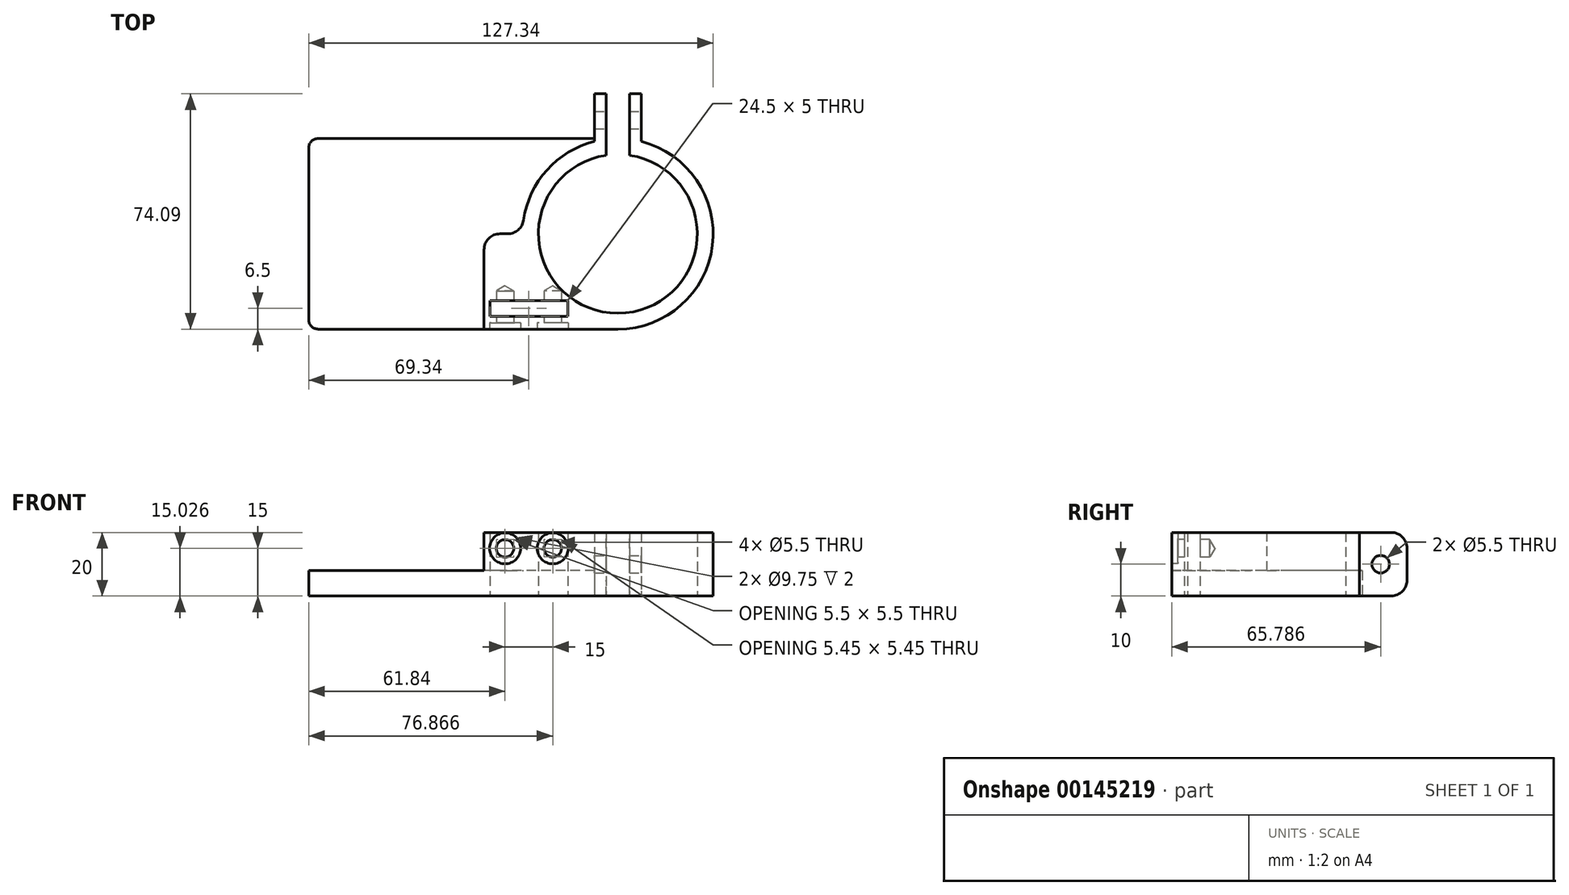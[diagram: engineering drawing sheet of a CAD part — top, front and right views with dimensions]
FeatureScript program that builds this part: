
annotation { "Feature Type Name" : "Feature", "Feature Type Description" : "" }
export const myFeature = defineFeature(function(context is Context, id is Id, definition is map)
    precondition{}
    {
        {
            var Q0;
            Q0=qCreatedBy(makeId("Top.planeOp"),FACE);
            var sketch = newSketch(context, id + "F0", { "sketchPlane" : qUnion([Q0])});
            skArc(sketch, "E0", {"start": v(-7.34, 29.09) * mm, "mid": v(0, -30) * mm, "end": v(7.34, 29.09) * mm});
            skArc(sketch, "E1.0", {"start": v(-3.67, 24.73) * mm, "mid": v(0, -25) * mm, "end": v(3.67, 24.73) * mm});
            skLineSegment(sketch, "E2", {"start": v(-7.34, 30) * mm, "end": v(-94.34, 30) * mm});
            skLineSegment(sketch, "E3", {"start": v(-97.34, 27) * mm, "end": v(-97.34, -27) * mm});
            skLineSegment(sketch, "E4", {"start": v(-94.34, -30) * mm, "end": v(0, -30) * mm});
            skLineSegment(sketch, "E5", {"start": v(-7.34, 29.09) * mm, "end": v(-7.34, 44.09) * mm});
            skLineSegment(sketch, "E6", {"start": v(-7.34, 44.09) * mm, "end": v(-3.67, 44.09) * mm});
            skLineSegment(sketch, "E7.MirrorCS", {"start": v(7.34, 29.09) * mm, "end": v(7.34, 44.09) * mm});
            skLineSegment(sketch, "E8.MirrorCS", {"start": v(7.34, 44.09) * mm, "end": v(3.67, 44.09) * mm});
            skPoint(sketch, "E9.orphan", {"position": v(0, 30) * mm});
            skPoint(sketch, "E10.orphan", {"position": v(-7.34, 23.9) * mm});
            skPoint(sketch, "E11.orphan", {"position": v(7.34, 23.9) * mm});
            skLineSegment(sketch, "E12", {"start": v(-3.67, 44.09) * mm, "end": v(-3.67, 24.73) * mm});
            skLineSegment(sketch, "E13.MirrorCS", {"start": v(3.67, 44.09) * mm, "end": v(3.67, 24.73) * mm});
            skPoint(sketch, "E14.orphan", {"position": v(0, 44.09) * mm});
            skPoint(sketch, "E15.visualSharp", {"position": v(-97.34, 30) * mm});
            skArc(sketch, "E15.filletArc", {"start": v(-94.34, 30) * mm, "mid": v(-96.46, 29.12) * mm, "end": v(-97.34, 27) * mm});
            skPoint(sketch, "E16.visualSharp", {"position": v(-97.34, -30) * mm});
            skArc(sketch, "E16.filletArc", {"start": v(-97.34, -27) * mm, "mid": v(-96.46, -29.12) * mm, "end": v(-94.34, -30) * mm});
            skPoint(sketch, "E17.start.orphan", {"position": v(-30, 0) * mm});
            skLineSegment(sketch, "E18", {"start": v(-30, 0) * mm, "end": v(-42.11, 0) * mm});
            skLineSegment(sketch, "E19", {"start": v(-42.11, 0) * mm, "end": v(-42.11, -30) * mm});
            skSolve(sketch);
        }
        {
            var Q0;
            Q0=makeQuery(id+"F0.imprint","IMPRINT",FACE,{"disambiguationData":[TD([[makeQuery(id+"F0.imprint","IMPRINT",EDGE,{"derivedFrom":sQuery(id+"F0.wireOp",EDGE,"E1.0")}),-1.0]])]});
            extrude(context, id + "F1", {"entities" : qUnion([Q0]), "depth" : 20 * mm});
        }
        {
            var Q0;
            Q0 = qSketchRegion(id + "F0", true);
            extrude(context, id + "F2", {"entities" : qUnion([Q0]), "operationType" : NewBodyOperationType.ADD, "depth" : 8 * mm});
        }
        {
            var Q0;
            {var subQ3=sQuery(id+"F0.wireOp",EDGE,"E18");Q0=makeQuery(id+"F0.imprint","IMPRINT",FACE,{"disambiguationData":[TD([[makeQuery(id+"F0.imprint","IMPRINT",EDGE,{"derivedFrom":subQ3}),1.0]])]});}
            extrude(context, id + "F3", {"entities" : qUnion([Q0]), "operationType" : NewBodyOperationType.ADD, "depth" : 20 * mm});
        }
        {
            var Q0;
            Q0=makeQuery(id+"F1.opExtrude","CAP_EDGE",EDGE,{"disambiguationData":[OSD([sQuery(id+"F0.wireOp",EDGE,"E8.MirrorCS")])],"isStart":true});
            var Q1;
            Q1=makeQuery(id+"F1.opExtrude","CAP_EDGE",EDGE,{"disambiguationData":[OSD([sQuery(id+"F0.wireOp",EDGE,"E6")])],"isStart":true});
            var Q2;
            Q2=makeQuery(id+"F1.opExtrude","CAP_EDGE",EDGE,{"disambiguationData":[OSD([sQuery(id+"F0.wireOp",EDGE,"E6")])],"isStart":false});
            var Q3;
            Q3=makeQuery(id+"F1.opExtrude","CAP_EDGE",EDGE,{"disambiguationData":[OSD([sQuery(id+"F0.wireOp",EDGE,"E8.MirrorCS")])],"isStart":false});
            fillet(context, id + "F4", {"entities" : qUnion([Q0, Q1, Q2, Q3]), "radius" : 5 * mm, "tangentPropagation" : true, "allowEdgeOverflow" : false});
        }
        {
            var Q0;
            Q0=makeQuery(id+"F1.opExtrude","SWEPT_FACE",FACE,{"disambiguationData":[OSD([sQuery(id+"F0.wireOp",EDGE,"E7.MirrorCS")])]});
            var sketch = newSketch(context, id + "F5", { "sketchPlane" : qUnion([Q0])});
            skPoint(sketch, "E20", {"position": v(35.79, 10) * mm});
            skPoint(sketch, "E20.positionSnap0", {"position": v(29.09, 10) * mm});
            skSolve(sketch);
        }
        {
            var Q0;
            Q0=sQuery(id+"F5.wireOp",VERTEX,"E20");
            var Q1;
            Q1=makeQuery(id+"F1.opExtrude","SWEPT_BODY",BODY,{"disambiguationData":[OSD([sQuery(id+"F0.wireOp",EDGE,"E0"),sQuery(id+"F0.wireOp",EDGE,"E1.0"),sQuery(id+"F0.wireOp",EDGE,"E5"),sQuery(id+"F0.wireOp",EDGE,"E6"),sQuery(id+"F0.wireOp",EDGE,"E7.MirrorCS"),sQuery(id+"F0.wireOp",EDGE,"E8.MirrorCS"),sQuery(id+"F0.wireOp",EDGE,"E12"),sQuery(id+"F0.wireOp",EDGE,"E13.MirrorCS")])]});
            hole(context, id + "F6", {"style" : HoleStyle.SIMPLE, "endStyle" : HoleEndStyle.THROUGH, "holeDiameter" : 5.5 * mm, "locations" : qUnion([Q0]), "scope" : qUnion([Q1]), "isTappedThrough" : true});
        }
        {
            var Q0;
            Q0=makeQuery(id+"F3.opExtrude","SWEPT_EDGE",EDGE,{"disambiguationData":[OSD([sQuery(id+"F0.wireOp",EDGE,"E18"),sQuery(id+"F0.wireOp",EDGE,"E19")])]});
            var Q1;
            Q1=makeQuery(id+"F3.opExtrude","SWEPT_EDGE",EDGE,{"disambiguationData":[OSD([sQuery(id+"F0.wireOp",EDGE,"E0"),sQuery(id+"F0.wireOp",EDGE,"E18")])]});
            fillet(context, id + "F7", {"entities" : qUnion([Q0, Q1]), "radius" : 5 * mm, "tangentPropagation" : true, "allowEdgeOverflow" : false});
        }
        {
            var Q0;
            {var subQ0=sQuery(id+"F0.wireOp",EDGE,"E13.MirrorCS");var subQ1=sQuery(id+"F0.wireOp",EDGE,"E12");var subQ2=sQuery(id+"F0.wireOp",EDGE,"E8.MirrorCS");var subQ3=sQuery(id+"F0.wireOp",EDGE,"E7.MirrorCS");var subQ4=sQuery(id+"F0.wireOp",EDGE,"E6");var subQ5=sQuery(id+"F0.wireOp",EDGE,"E5");var subQ6=sQuery(id+"F0.wireOp",EDGE,"E1.0");var subQ7=sQuery(id+"F0.wireOp",EDGE,"E0");Q0=makeQuery(id+"F2.boolean.opBoolean","MERGE",FACE,{"derivedFrom":[makeQuery(id+"F1.opExtrude","CAP_FACE",FACE,{"disambiguationData":[OSD([subQ7,subQ6,subQ5,subQ4,subQ3,subQ2,subQ1,subQ0])],"isStart":true}),makeQuery(id+"F2.opExtrude","CAP_FACE",FACE,{"disambiguationData":[OSD([subQ7,subQ6,sQuery(id+"F0.wireOp",EDGE,"E2"),sQuery(id+"F0.wireOp",EDGE,"E3"),sQuery(id+"F0.wireOp",EDGE,"E4"),subQ5,subQ4,subQ3,subQ2,subQ1,subQ0,sQuery(id+"F0.wireOp",EDGE,"E15.filletArc"),sQuery(id+"F0.wireOp",EDGE,"E16.filletArc")])],"isStart":true})]});}
            var sketch = newSketch(context, id + "F8", { "sketchPlane" : qUnion([Q0])});
            skLineSegment(sketch, "E21.bottom", {"start": v(-40.25, 26) * mm, "end": v(-15.75, 26) * mm});
            skLineSegment(sketch, "E21.top", {"start": v(-40.25, 21) * mm, "end": v(-15.75, 21) * mm});
            skLineSegment(sketch, "E21.left", {"start": v(-40.25, 26) * mm, "end": v(-40.25, 21) * mm});
            skLineSegment(sketch, "E21.right", {"start": v(-15.75, 26) * mm, "end": v(-15.75, 21) * mm});
            skLineSegment(sketch, "E22", {"start": v(-28, 43.68) * mm, "end": v(-28, 10.05) * mm, "construction": true});
            skPoint(sketch, "E22.startSnap0", {"position": v(-28, 26) * mm});
            skSolve(sketch);
        }
        {
            var Q0;
            Q0=makeQuery(id+"F8.imprint","IMPRINT",FACE,{"disambiguationData":[TD([[makeQuery(id+"F8.imprint","IMPRINT",EDGE,{"derivedFrom":sQuery(id+"F8.wireOp",EDGE,"E21.bottom")}),-1.0]])]});
            extrude(context, id + "F9", {"entities" : qUnion([Q0]), "operationType" : NewBodyOperationType.REMOVE, "oppositeDirection" : true, "depth" : 25 * mm});
        }
        {
            var Q0;
            {var subQ0=sQuery(id+"F0.wireOp",EDGE,"E4");Q0=makeQuery(id+"F3.boolean.opBoolean","MERGE",FACE,{"derivedFrom":[makeQuery(id+"F2.opExtrude","SWEPT_FACE",FACE,{"disambiguationData":[OSD([subQ0])]}),makeQuery(id+"F3.opExtrude","SWEPT_FACE",FACE,{"disambiguationData":[OSD([subQ0])]})]});}
            var sketch = newSketch(context, id + "F10", { "sketchPlane" : qUnion([Q0])});
            skLineSegment(sketch, "E23", {"start": v(-0.46, 15) * mm, "end": v(-42.78, 15) * mm, "construction": true});
            skLineSegment(sketch, "E24", {"start": v(-28, 39.47) * mm, "end": v(-28, -15.67) * mm, "construction": true});
            skPoint(sketch, "E25", {"position": v(-35.5, 15) * mm});
            skPoint(sketch, "E26.MirrorP", {"position": v(-20.5, 15) * mm});
            skSolve(sketch);
        }
        {
            var Q0;
            Q0=sQuery(id+"F10.wireOp",VERTEX,"E25");
            var Q1;
            Q1=sQuery(id+"F10.wireOp",VERTEX,"E26.MirrorP");
            var Q2;
            Q2=makeQuery(id+"F1.opExtrude","SWEPT_BODY",BODY,{"disambiguationData":[OSD([sQuery(id+"F0.wireOp",EDGE,"E0"),sQuery(id+"F0.wireOp",EDGE,"E1.0"),sQuery(id+"F0.wireOp",EDGE,"E5"),sQuery(id+"F0.wireOp",EDGE,"E6"),sQuery(id+"F0.wireOp",EDGE,"E7.MirrorCS"),sQuery(id+"F0.wireOp",EDGE,"E8.MirrorCS"),sQuery(id+"F0.wireOp",EDGE,"E12"),sQuery(id+"F0.wireOp",EDGE,"E13.MirrorCS")])]});
            hole(context, id + "F11", {"style" : HoleStyle.C_BORE, "endStyle" : HoleEndStyle.BLIND, "holeDiameter" : 5.5 * mm, "cBoreDiameter" : 9.75 * mm, "cBoreDepth" : 2 * mm, "holeDepth" : 12 * mm, "locations" : qUnion([Q0, Q1]), "scope" : qUnion([Q2])});
        }
    });
